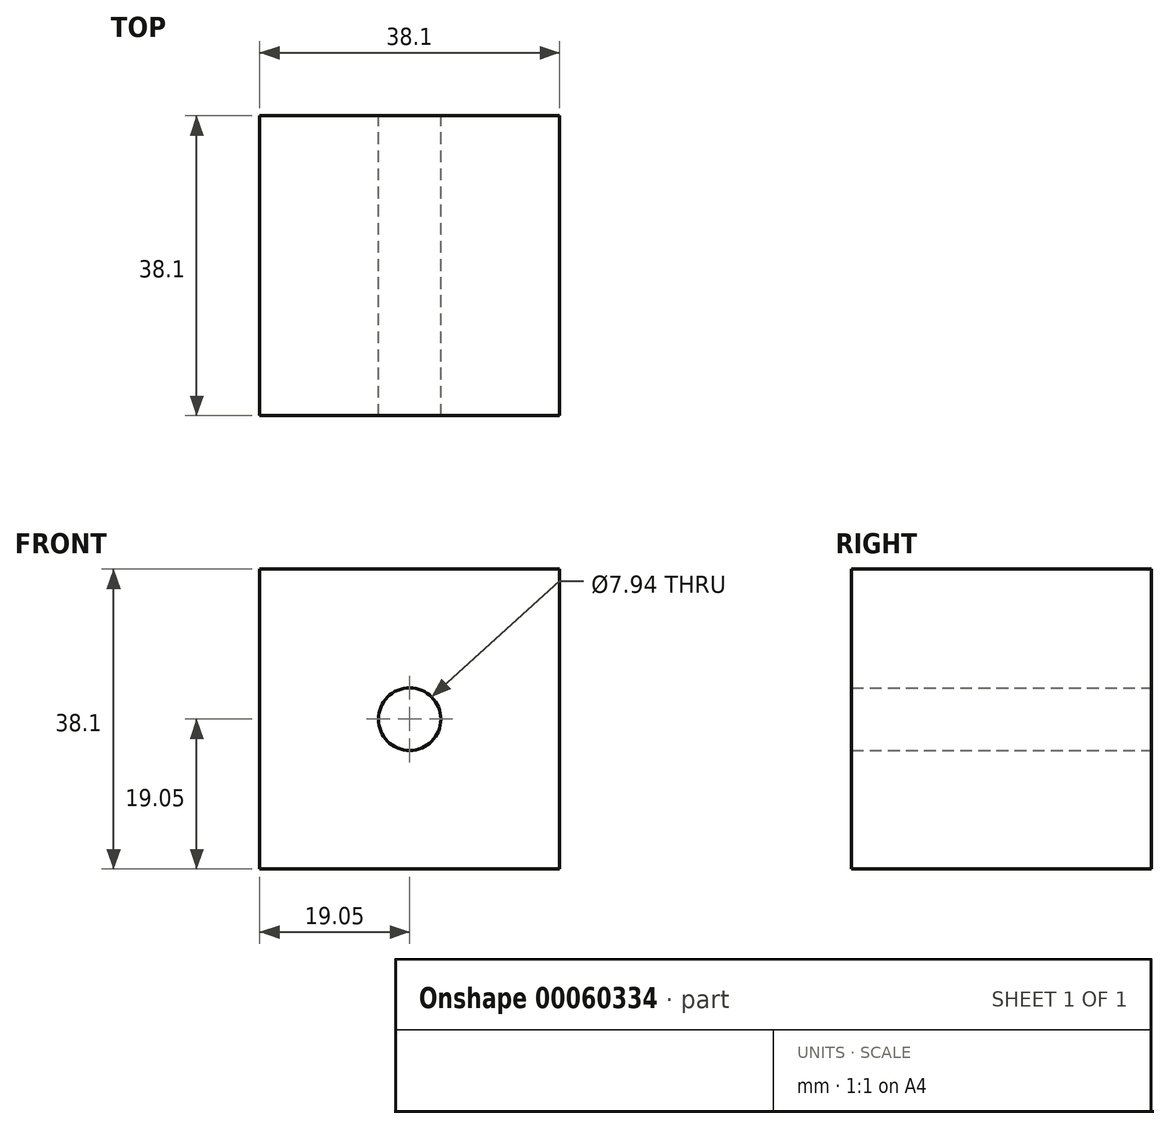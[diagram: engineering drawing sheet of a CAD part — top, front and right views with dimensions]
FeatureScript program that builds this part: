
annotation { "Feature Type Name" : "Feature", "Feature Type Description" : "" }
export const myFeature = defineFeature(function(context is Context, id is Id, definition is map)
    precondition{}
    {
        {
            var Q0;
            Q0=qCreatedBy(makeId("Front.planeOp"),FACE);
            var sketch = newSketch(context, id + "F0", { "sketchPlane" : qUnion([Q0])});
            skLineSegment(sketch, "E0.rect.bottom", {"start": v(-19.05, 19.05) * mm, "end": v(19.05, 19.05) * mm});
            skLineSegment(sketch, "E0.rect.top", {"start": v(-19.05, -19.05) * mm, "end": v(19.05, -19.05) * mm});
            skLineSegment(sketch, "E0.rect.left", {"start": v(-19.05, 19.05) * mm, "end": v(-19.05, -19.05) * mm});
            skLineSegment(sketch, "E0.rect.right", {"start": v(19.05, 19.05) * mm, "end": v(19.05, -19.05) * mm});
            skPoint(sketch, "E0.rect.middle", {"position": v(0, 0) * mm});
            skCircle(sketch, "E1", {"center": v(0, 0) * mm, "radius": 3.97 * mm});
            skSolve(sketch);
        }
        {
            var Q0;
            Q0 = qSketchRegion(id + "F0", true);
            extrude(context, id + "F1", {"entities" : qUnion([Q0]), "depth" : 38.1 * mm});
        }
    });
